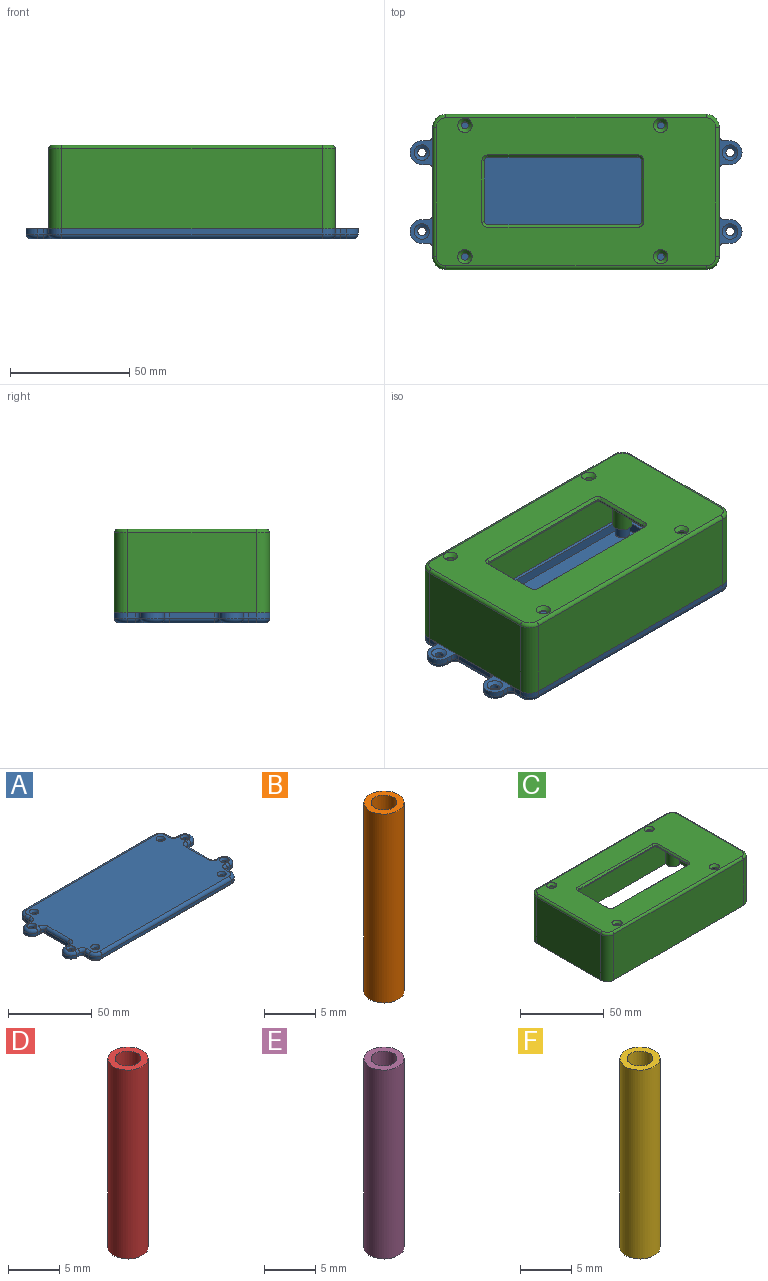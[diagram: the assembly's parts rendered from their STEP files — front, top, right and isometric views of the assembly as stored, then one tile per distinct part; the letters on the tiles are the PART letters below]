
ASSEMBLY  parts=6 mates=1
PART A: 112 faces, bbox 139.8x65.9x6.2 mm
  f0: plane 3.5x2.2mm, normal (-1,0,0), area 7.7mm2, adj f8,f14,f60,f96
  f1: plane 3.5x2.2mm, normal (-1,0,0), area 7.7mm2, adj f10,f14,f63,f72
  f2: plane 3.5x2.2mm, normal (1,0,0), area 7.7mm2, adj f6,f14,f64,f95
  f3: plane 19x2.2mm, normal (1,0,0), area 41.8mm2, adj f14,f65,f66,f83
  f4: plane 113.4x58.4mm, normal (0,0,-1), area 6505.3mm2, adj f15,f16,f17,f18,f19,f20,f21,f22
  f5: plane 135x61mm, normal (0,0,1), area 7115.4mm2, adj f68,f69,f70,f71,f72,f73,f74,f75
  f6: cylinder r=5.5mm len=5.5mm, axis (0,0,1), area 19mm2, adj f2,f7,f14,f97
  f7: plane 109x2.2mm, normal (0,1,0), area 239.8mm2, adj f6,f8,f14,f99
  f8: cylinder r=5.5mm len=5.5mm, axis (0,0,1), area 19mm2, adj f0,f7,f14,f98
  f9: plane 19x2.2mm, normal (-1,0,0), area 41.8mm2, adj f14,f61,f62,f84
  f10: cylinder r=5.5mm len=5.5mm, axis (0,0,1), area 19mm2, adj f1,f11,f14,f70
  f11: plane 109x2.2mm, normal (0,-1,0), area 239.8mm2, adj f10,f12,f14,f68
  f12: cylinder r=5.5mm len=5.5mm, axis (0,0,1), area 19mm2, adj f11,f13,f14,f69
  f13: plane 3.5x2.2mm, normal (1,0,0), area 7.7mm2, adj f12,f14,f67,f71
  f14: plane 139x65mm, normal (0,0,-1), area 832.6mm2, adj f0,f1,f2,f3,f6,f7,f8,f9
  f15: cylinder r=2.2mm len=4.2mm, axis (0,0,1), area 14.5mm2, adj f4,f16,f22,f31
  f16: plane 54x4.2mm, normal (-1,0,0), area 226.8mm2, adj f4,f15,f17,f31
  f17: cylinder r=2.2mm len=4.2mm, axis (0,0,1), area 14.5mm2, adj f4,f16,f18,f31
  f18: plane 109x4.2mm, normal (0,1,0), area 457.8mm2, adj f4,f17,f19,f31
  f19: cylinder r=2.2mm len=4.2mm, axis (0,0,1), area 14.5mm2, adj f4,f18,f20,f31
  f20: plane 54x4.2mm, normal (1,0,0), area 226.8mm2, adj f4,f19,f21,f31
  f21: cylinder r=2.2mm len=4.2mm, axis (0,0,1), area 14.5mm2, adj f4,f20,f22,f31
  f22: plane 109x4.2mm, normal (0,-1,0), area 457.8mm2, adj f4,f15,f21,f31
  f23: plane 54x2mm, normal (1,0,0), area 108mm2, adj f14,f24,f30,f31
  f24: cylinder r=3.75mm len=3.75mm, axis (0,0,1), area 11.8mm2, adj f14,f23,f25,f31
  f25: plane 109x2mm, normal (0,1,0), area 218mm2, adj f14,f24,f26,f31
  f26: cylinder r=3.75mm len=3.75mm, axis (0,0,1), area 11.8mm2, adj f14,f25,f27,f31
  f27: plane 54x2mm, normal (-1,0,0), area 108mm2, adj f14,f26,f28,f31
  f28: cylinder r=3.75mm len=3.75mm, axis (0,0,1), area 11.8mm2, adj f14,f27,f29,f31
  f29: plane 109x2mm, normal (0,-1,0), area 218mm2, adj f14,f28,f30,f31
  f30: cylinder r=3.75mm len=3.75mm, axis (0,0,1), area 11.8mm2, adj f14,f23,f29,f31
  f31: plane 116.5x61.5mm, normal (0,0,-1), area 534.3mm2, adj f15,f16,f17,f18,f19,f20,f21,f22
  f32: plane 6x6mm, normal (0,0,-1), area 18.7mm2, adj f33,f43
  f33: cylinder r=3mm len=6mm, axis (0,0,1), area 79.2mm2, adj f4,f32
  f34: plane 6x6mm, normal (0,0,-1), area 18.7mm2, adj f35,f42
  f35: cylinder r=3mm len=6mm, axis (0,0,1), area 79.2mm2, adj f4,f34
  f36: plane 6x6mm, normal (0,0,-1), area 18.7mm2, adj f37,f41
  f37: cylinder r=3mm len=6mm, axis (0,0,1), area 79.2mm2, adj f4,f36
  f38: plane 6x6mm, normal (0,0,-1), area 18.7mm2, adj f39,f40
  f39: cylinder r=3mm len=6mm, axis (0,0,1), area 79.2mm2, adj f4,f38
  f40: cylinder r=1.75mm len=4.47mm, axis (0,0,1), area 49.1mm2, adj f38,f100
  f41: cylinder r=1.75mm len=4.47mm, axis (0,0,1), area 49.1mm2, adj f36,f102
  f42: cylinder r=1.75mm len=4.47mm, axis (0,0,1), area 49.1mm2, adj f34,f103
  f43: cylinder r=1.75mm len=4.47mm, axis (0,0,1), area 49.1mm2, adj f32,f101
  f44: plane 2.5x2.2mm, normal (0,1,0), area 5.5mm2, adj f14,f46,f66,f79
  f45: plane 2.5x2.2mm, normal (0,-1,0), area 5.5mm2, adj f14,f46,f67,f75
  f46: cylinder r=5mm len=10mm, axis (0,0,1), area 34.6mm2, adj f14,f44,f45,f77
  f47: cylinder r=1.75mm len=3.5mm, axis (0,0,1), area 18.7mm2, adj f104,f109
  f48: plane 2.5x2.2mm, normal (0,1,0), area 5.5mm2, adj f14,f51,f64,f91
  f49: plane 2.5x2.2mm, normal (0,-1,0), area 5.5mm2, adj f14,f51,f65,f87
  f50: cylinder r=1.75mm len=3.5mm, axis (0,0,1), area 18.7mm2, adj f105,f108
  f51: cylinder r=5mm len=10mm, axis (0,0,1), area 34.6mm2, adj f14,f48,f49,f89
  f52: plane 2.5x2.2mm, normal (0,1,0), area 5.5mm2, adj f14,f54,f62,f80
  f53: cylinder r=1.75mm len=3.5mm, axis (0,0,1), area 18.7mm2, adj f107,f110
  f54: cylinder r=5mm len=10mm, axis (0,0,1), area 34.6mm2, adj f14,f52,f55,f78
  f55: plane 2.5x2.2mm, normal (0,-1,0), area 5.5mm2, adj f14,f54,f63,f76
  f56: plane 2.5x2.2mm, normal (0,1,0), area 5.5mm2, adj f14,f57,f60,f92
  f57: cylinder r=5mm len=10mm, axis (0,0,1), area 34.6mm2, adj f14,f56,f58,f90
  f58: plane 2.5x2.2mm, normal (0,-1,0), area 5.5mm2, adj f14,f57,f61,f88
  f59: cylinder r=1.75mm len=3.5mm, axis (0,0,1), area 18.7mm2, adj f106,f111
  f60: cylinder r=2mm len=2.2mm, axis (0,0,-1), area 6.9mm2, adj f0,f14,f56,f94
  f61: cylinder r=2mm len=2.2mm, axis (0,0,1), area 6.9mm2, adj f9,f14,f58,f86
  f62: cylinder r=2mm len=2.2mm, axis (0,0,-1), area 6.9mm2, adj f9,f14,f52,f82
  f63: cylinder r=2mm len=2.2mm, axis (0,0,1), area 6.9mm2, adj f1,f14,f55,f74
  f64: cylinder r=2mm len=2.2mm, axis (0,0,-1), area 6.9mm2, adj f2,f14,f48,f93
  f65: cylinder r=2mm len=2.2mm, axis (0,0,1), area 6.9mm2, adj f3,f14,f49,f85
  f66: cylinder r=2mm len=2.2mm, axis (0,0,-1), area 6.9mm2, adj f3,f14,f44,f81
  f67: cylinder r=2mm len=2.2mm, axis (0,0,1), area 6.9mm2, adj f13,f14,f45,f73
  f68: cylinder r=2mm len=109mm, axis (1,0,0), area 342.4mm2, adj f5,f11,f69,f70
  f69: torus R=3.5mm, axis (0,0,1), area 23.6mm2, adj f5,f12,f68,f71
  f70: torus R=3.5mm, axis (0,0,1), area 23.6mm2, adj f5,f10,f68,f72
  f71: cylinder r=2mm len=3.5mm, axis (0,1,0), area 11mm2, adj f5,f13,f69,f73
  f72: cylinder r=2mm len=3.5mm, axis (0,-1,0), area 11mm2, adj f1,f5,f70,f74
  f73: torus R=4mm, axis (0,0,1), area 13.5mm2, adj f5,f67,f71,f75
  f74: torus R=4mm, axis (0,0,1), area 13.5mm2, adj f5,f63,f72,f76
  f75: cylinder r=2mm len=2.5mm, axis (1,0,0), area 7.9mm2, adj f5,f45,f73,f77
  f76: cylinder r=2mm len=2.5mm, axis (1,0,0), area 7.9mm2, adj f5,f55,f74,f78
  f77: torus R=3mm, axis (0,0,1), area 42.2mm2, adj f5,f46,f75,f79
  f78: torus R=3mm, axis (0,0,1), area 42.2mm2, adj f5,f54,f76,f80
  f79: cylinder r=2mm len=2.5mm, axis (-1,0,0), area 7.9mm2, adj f5,f44,f77,f81
  f80: cylinder r=2mm len=2.5mm, axis (-1,0,0), area 7.9mm2, adj f5,f52,f78,f82
  f81: torus R=4mm, axis (0,0,1), area 13.5mm2, adj f5,f66,f79,f83
  f82: torus R=4mm, axis (0,0,1), area 13.5mm2, adj f5,f62,f80,f84
  f83: cylinder r=2mm len=19mm, axis (0,1,0), area 59.7mm2, adj f3,f5,f81,f85
  f84: cylinder r=2mm len=19mm, axis (0,-1,0), area 59.7mm2, adj f5,f9,f82,f86
  f85: torus R=4mm, axis (0,0,1), area 13.5mm2, adj f5,f65,f83,f87
  f86: torus R=4mm, axis (0,0,1), area 13.5mm2, adj f5,f61,f84,f88
  f87: cylinder r=2mm len=2.5mm, axis (1,0,0), area 7.9mm2, adj f5,f49,f85,f89
  f88: cylinder r=2mm len=2.5mm, axis (1,0,0), area 7.9mm2, adj f5,f58,f86,f90
  f89: torus R=3mm, axis (0,0,1), area 42.2mm2, adj f5,f51,f87,f91
  f90: torus R=3mm, axis (0,0,1), area 42.2mm2, adj f5,f57,f88,f92
  f91: cylinder r=2mm len=2.5mm, axis (-1,0,0), area 7.9mm2, adj f5,f48,f89,f93
  f92: cylinder r=2mm len=2.5mm, axis (-1,0,0), area 7.9mm2, adj f5,f56,f90,f94
  f93: torus R=4mm, axis (0,0,1), area 13.5mm2, adj f5,f64,f91,f95
  f94: torus R=4mm, axis (0,0,1), area 13.5mm2, adj f5,f60,f92,f96
  f95: cylinder r=2mm len=3.5mm, axis (0,1,0), area 11mm2, adj f2,f5,f93,f97
  f96: cylinder r=2mm len=3.5mm, axis (0,-1,0), area 11mm2, adj f0,f5,f94,f98
  f97: torus R=3.5mm, axis (0,0,1), area 23.6mm2, adj f5,f6,f95,f99
  f98: torus R=3.5mm, axis (0,0,1), area 23.6mm2, adj f5,f8,f96,f99
  f99: cylinder r=2mm len=109mm, axis (-1,0,0), area 342.4mm2, adj f5,f7,f97,f98
  f100: cone r=2.75mm half-angle=30deg, axis (0,0,1), area 28.3mm2, adj f5,f40
  f101: cone r=2.75mm half-angle=30deg, axis (0,0,1), area 28.3mm2, adj f5,f43
  f102: cone r=2.75mm half-angle=30deg, axis (0,0,1), area 28.3mm2, adj f5,f41
  f103: cone r=2.75mm half-angle=30deg, axis (0,0,1), area 28.3mm2, adj f5,f42
  f104: cone r=2.75mm half-angle=33.7deg, axis (0,0,1), area 25.5mm2, adj f5,f47
  f105: cone r=1.75mm half-angle=33.7deg, axis (0,0,1), area 25.5mm2, adj f5,f50
  f106: cone r=2.75mm half-angle=33.7deg, axis (0,0,1), area 25.5mm2, adj f5,f59
  f107: cone r=1.75mm half-angle=33.7deg, axis (0,0,1), area 25.5mm2, adj f5,f53
  f108: cone r=1.75mm half-angle=56.3deg, axis (0,0,-1), area 28.3mm2, adj f14,f50
  f109: cone r=3.25mm half-angle=56.3deg, axis (0,0,-1), area 28.3mm2, adj f14,f47
  f110: cone r=1.75mm half-angle=56.3deg, axis (0,0,-1), area 28.3mm2, adj f14,f53
  f111: cone r=3.25mm half-angle=56.3deg, axis (0,0,-1), area 28.3mm2, adj f14,f59
PART B: 4 faces, bbox 3.9x3.9x22.5 mm
  f0: plane 3.9x3.9mm, normal (0,0,-1), area 7mm2, adj f1,f2
  f1: cylinder r=1.25mm len=22.5mm, axis (0,0,1), area 176.7mm2, adj f0,f3
  f2: cylinder r=1.95mm len=22.5mm, axis (0,0,1), area 275.7mm2, adj f0,f3
  f3: plane 3.9x3.9mm, normal (0,0,1), area 7mm2, adj f1,f2
PART C: 79 faces, bbox 120.9x65.9x35 mm
  f0: plane 117x62mm, normal (0,0,1), area 5078.2mm2, adj f47,f48,f49,f50,f51,f52,f53,f54
  f1: plane 116.5x61.5mm, normal (0,0,-1), area 5054mm2, adj f11,f12,f13,f14,f15,f16,f17,f18
  f2: plane 120x65mm, normal (0,0,-1), area 621.4mm2, adj f3,f4,f5,f6,f7,f8,f9,f10
  f3: plane 109x33.5mm, normal (0,-1,0), area 3651.5mm2, adj f2,f4,f10,f54
  f4: cylinder r=5.5mm len=33.5mm, axis (0,0,1), area 289.4mm2, adj f2,f3,f5,f52
  f5: plane 54x33.5mm, normal (1,0,0), area 1809mm2, adj f2,f4,f6,f50
  f6: cylinder r=5.5mm len=33.5mm, axis (0,0,1), area 289.4mm2, adj f2,f5,f7,f48
  f7: plane 109x33.5mm, normal (0,1,0), area 3651.5mm2, adj f2,f6,f8,f47
  f8: cylinder r=5.5mm len=33.5mm, axis (0,0,1), area 289.4mm2, adj f2,f7,f9,f49
  f9: plane 54x33.5mm, normal (-1,0,0), area 1809mm2, adj f2,f8,f10,f51
  f10: cylinder r=5.5mm len=33.5mm, axis (0,0,1), area 289.4mm2, adj f2,f3,f9,f53
  f11: plane 109x33.25mm, normal (0,1,0), area 3624.3mm2, adj f1,f2,f12,f18
  f12: cylinder r=3.75mm len=33.25mm, axis (0,0,1), area 150.9mm2, adj f1,f2,f11,f13,f38,f39,f40
  f13: plane 54x33.25mm, normal (-1,0,0), area 1795.5mm2, adj f1,f2,f12,f14
  f14: cylinder r=3.75mm len=33.25mm, axis (0,0,1), area 150.9mm2, adj f1,f2,f13,f15,f44,f45,f46
  f15: plane 109x33.25mm, normal (0,-1,0), area 3624.3mm2, adj f1,f2,f14,f16
  f16: cylinder r=3.75mm len=33.25mm, axis (0,0,1), area 150.9mm2, adj f1,f2,f15,f17,f41,f42,f43
  f17: plane 54x33.25mm, normal (1,0,0), area 1795.5mm2, adj f1,f2,f16,f18
  f18: cylinder r=3.75mm len=33.25mm, axis (0,0,1), area 150.9mm2, adj f1,f2,f11,f17,f35,f36,f37
  f19: cylinder r=1.95mm len=30.75mm, axis (0,0,1), area 376.8mm2, adj f21,f22
  f20: cylinder r=4mm len=30.75mm, axis (0,0,1), area 727.9mm2, adj f1,f21,f44,f45,f46
  f21: plane 8x8mm, normal (0,0,-1), area 38.3mm2, adj f19,f20
  f22: plane 3.9x3.9mm, normal (0,0,-1), area 11.9mm2, adj f19
  f23: cylinder r=1.95mm len=30.75mm, axis (0,0,1), area 376.8mm2, adj f25,f26
  f24: cylinder r=4mm len=30.75mm, axis (0,0,1), area 727.9mm2, adj f1,f25,f41,f42,f43
  f25: plane 8x8mm, normal (0,0,-1), area 38.3mm2, adj f23,f24
  f26: plane 3.9x3.9mm, normal (0,0,-1), area 11.9mm2, adj f23
  f27: cylinder r=1.95mm len=30.75mm, axis (0,0,1), area 376.8mm2, adj f29,f30
  f28: cylinder r=4mm len=30.75mm, axis (0,0,1), area 727.9mm2, adj f1,f29,f35,f36,f37
  f29: plane 8x8mm, normal (0,0,-1), area 38.3mm2, adj f27,f28
  f30: plane 3.9x3.9mm, normal (0,0,-1), area 11.9mm2, adj f27
  f31: cylinder r=1.95mm len=30.75mm, axis (0,0,1), area 376.8mm2, adj f33,f34
  f32: cylinder r=4mm len=30.75mm, axis (0,0,1), area 727.9mm2, adj f1,f33,f38,f39,f40
  f33: plane 8x8mm, normal (0,0,-1), area 38.3mm2, adj f31,f32
  f34: plane 3.9x3.9mm, normal (0,0,-1), area 11.9mm2, adj f31
  f35: plane 2.13x2.13mm, normal (0,0,-1), area 2.3mm2, adj f18,f28,f36,f37
  f36: plane 29.75x1.07mm, normal (-0.71,0.71,0), area 45mm2, adj f1,f18,f28,f35
  f37: plane 29.75x1.07mm, normal (0.71,-0.71,0), area 45mm2, adj f1,f18,f28,f35
  f38: plane 2.13x2.13mm, normal (0,0,-1), area 2.3mm2, adj f12,f32,f39,f40
  f39: plane 29.75x1.07mm, normal (0.71,0.71,0), area 45mm2, adj f1,f12,f32,f38
  f40: plane 29.75x1.07mm, normal (-0.71,-0.71,0), area 45mm2, adj f1,f12,f32,f38
  f41: plane 2.13x2.13mm, normal (0,0,-1), area 2.3mm2, adj f16,f24,f42,f43
  f42: plane 29.75x1.07mm, normal (-0.71,-0.71,0), area 45mm2, adj f1,f16,f24,f41
  f43: plane 29.75x1.07mm, normal (0.71,0.71,0), area 45mm2, adj f1,f16,f24,f41
  f44: plane 2.13x2.13mm, normal (0,0,-1), area 2.3mm2, adj f14,f20,f45,f46
  f45: plane 29.75x1.07mm, normal (0.71,-0.71,0), area 45mm2, adj f1,f14,f20,f44
  f46: plane 29.75x1.07mm, normal (-0.71,0.71,0), area 45mm2, adj f1,f14,f20,f44
  f47: cylinder r=1.5mm len=109mm, axis (-1,0,0), area 256.8mm2, adj f0,f7,f48,f49
  f48: torus R=4mm, axis (0,0,1), area 18.3mm2, adj f0,f6,f47,f50
  f49: torus R=4mm, axis (0,0,1), area 18.3mm2, adj f0,f8,f47,f51
  f50: cylinder r=1.5mm len=54mm, axis (0,1,0), area 127.2mm2, adj f0,f5,f48,f52
  f51: cylinder r=1.5mm len=54mm, axis (0,-1,0), area 127.2mm2, adj f0,f9,f49,f53
  f52: torus R=4mm, axis (0,0,1), area 18.3mm2, adj f0,f4,f50,f54
  f53: torus R=4mm, axis (0,0,1), area 18.3mm2, adj f0,f10,f51,f54
  f54: cylinder r=1.5mm len=109mm, axis (1,0,0), area 256.8mm2, adj f0,f3,f52,f53
  f55: plane 62.8x0.75mm, normal (0,-1,0), area 47.1mm2, adj f1,f67,f70,f71
  f56: plane 25.3x0.75mm, normal (1,0,0), area 19mm2, adj f1,f67,f68,f74
  f57: plane 62.8x0.75mm, normal (0,1,0), area 47.1mm2, adj f1,f68,f69,f78
  f58: plane 25.3x0.75mm, normal (-1,0,0), area 19mm2, adj f1,f69,f70,f75
  f59: cylinder r=1.5mm len=3mm, axis (0,0,1), area 2.4mm2, adj f1,f66
  f60: cylinder r=1.5mm len=3mm, axis (0,0,1), area 2.4mm2, adj f1,f64
  f61: cylinder r=1.5mm len=3mm, axis (0,0,1), area 2.4mm2, adj f1,f63
  f62: cylinder r=1.5mm len=3mm, axis (0,0,1), area 2.4mm2, adj f1,f65
  f63: cone r=1.5mm half-angle=45deg, axis (0,0,1), area 30mm2, adj f0,f61
  f64: cone r=1.5mm half-angle=45deg, axis (0,0,1), area 30mm2, adj f0,f60
  f65: cone r=1.5mm half-angle=45deg, axis (0,0,1), area 30mm2, adj f0,f62
  f66: cone r=1.5mm half-angle=45deg, axis (0,0,1), area 30mm2, adj f0,f59
  f67: cylinder r=1.5mm len=1.5mm, axis (0,0,1), area 1.8mm2, adj f1,f55,f56,f72
  f68: cylinder r=1.5mm len=1.5mm, axis (0,0,-1), area 1.8mm2, adj f1,f56,f57,f76
  f69: cylinder r=1.5mm len=1.5mm, axis (0,0,1), area 1.8mm2, adj f1,f57,f58,f77
  f70: cylinder r=1.5mm len=1.5mm, axis (0,0,-1), area 1.8mm2, adj f1,f55,f58,f73
  f71: plane 62.8x1mm, normal (0,-0.71,0.71), area 88.8mm2, adj f0,f55,f72,f73
  f72: cone r=2.5mm half-angle=45deg, axis (0,0,1), area 4.4mm2, adj f0,f67,f71,f74
  f73: cone r=2.5mm half-angle=45deg, axis (0,0,1), area 4.4mm2, adj f0,f70,f71,f75
  f74: plane 25.3x1mm, normal (0.71,0,0.71), area 35.8mm2, adj f0,f56,f72,f76
  f75: plane 25.3x1mm, normal (-0.71,0,0.71), area 35.8mm2, adj f0,f58,f73,f77
  f76: cone r=2.5mm half-angle=45deg, axis (0,0,1), area 4.4mm2, adj f0,f68,f74,f78
  f77: cone r=2.5mm half-angle=45deg, axis (0,0,1), area 4.4mm2, adj f0,f69,f75,f78
  f78: plane 62.8x1mm, normal (0,0.71,0.71), area 88.8mm2, adj f0,f57,f76,f77
PART D: 4 faces, bbox 3.9x3.9x22.5 mm
  f0: plane 3.9x3.9mm, normal (0,0,-1), area 7mm2, adj f1,f2
  f1: cylinder r=1.25mm len=22.5mm, axis (0,0,1), area 176.7mm2, adj f0,f3
  f2: cylinder r=1.95mm len=22.5mm, axis (0,0,1), area 275.7mm2, adj f0,f3
  f3: plane 3.9x3.9mm, normal (0,0,1), area 7mm2, adj f1,f2
PART E: 4 faces, bbox 3.9x3.9x22.5 mm
  f0: plane 3.9x3.9mm, normal (0,0,-1), area 7mm2, adj f1,f2
  f1: cylinder r=1.25mm len=22.5mm, axis (0,0,1), area 176.7mm2, adj f0,f3
  f2: cylinder r=1.95mm len=22.5mm, axis (0,0,1), area 275.7mm2, adj f0,f3
  f3: plane 3.9x3.9mm, normal (0,0,1), area 7mm2, adj f1,f2
PART F: 4 faces, bbox 3.9x3.9x22.5 mm
  f0: plane 3.9x3.9mm, normal (0,0,-1), area 7mm2, adj f1,f2
  f1: cylinder r=1.25mm len=22.5mm, axis (0,0,1), area 176.7mm2, adj f0,f3
  f2: cylinder r=1.95mm len=22.5mm, axis (0,0,1), area 275.7mm2, adj f0,f3
  f3: plane 3.9x3.9mm, normal (0,0,1), area 7mm2, adj f1,f2
PLACE A rot(axis=(0,1,0),180deg) t=(-9.9,-16.82,-77.75)mm
PLACE B t=(-9.9,-16.82,11.45)mm fixed
PLACE C t=(-9.9,-16.82,11.45)mm fixed
PLACE D t=(-9.9,-16.82,11.45)mm fixed
PLACE E t=(-9.9,-16.82,11.45)mm fixed
PLACE F t=(-9.9,-16.82,11.45)mm fixed
MATE fastened A.f14 <-> C.f2  axis (0,0,1) through (-9.9,-16.82,-23.55)mm
